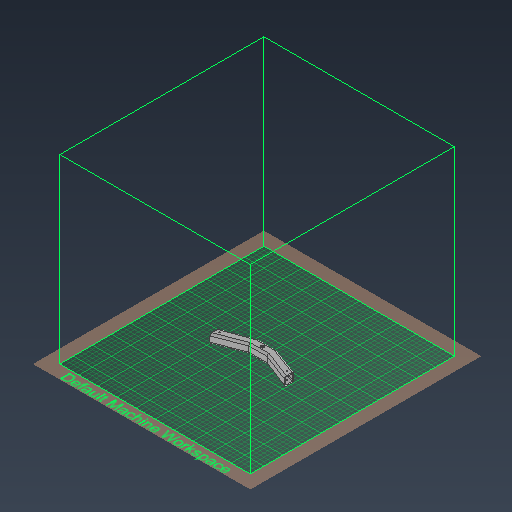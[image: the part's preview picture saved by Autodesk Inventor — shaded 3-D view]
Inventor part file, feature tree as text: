
AUTODESK INVENTOR PART (.ipt)
format: ipt  version: 2021 (Build 250183000, 183)  size: 565,760 bytes
history: native  units: mm
features: extrude x10, sketch x10, fillet x2, shell x1
ambient origin geometry x8: Origin, YZ Plane, XZ Plane, XY Plane, X Axis, Y Axis, Z Axis, Center Point
bodies: Volumenkörper1 (feature_tree)
feature tree (23):
  extrude  "Extrusion1"  Depth=66.0mm
  fillet  "Rundung3"  Radius=66.0mm
  shell  "Wandung3"  Thickness=3.490659mm
  extrude  "Extrusion8"  Depth=20.0mm
  extrude  "Extrusion9"  Depth=12.0mm
  extrude  "Extrusion10"  Depth=15.0mm
  fillet  "Rundung7"  Radius=3.0mm
  extrude  "Extrusion14"  Depth=12.0mm
  extrude  "Extrusion17"  Depth=3.0mm TaperAngle=0.0deg
  extrude  "Extrusion18"  Depth=12.0mm
  extrude  "Extrusion19"  Depth=12.0mm
  extrude  "Extrusion20"  Depth=3.0mm
  extrude  "Extrusion21"  Depth=8.5mm
  sketch  "Skizze1"  dims[d0=40.0mm d3=66.0mm d7=66.0mm d8=3.490659mm]
  sketch  "Skizze6"  dims[d9=20.0mm d10=0.0mm d19=4.0mm]
  sketch  "Skizze7"  dims[d48=2.6mm d51=12.0mm]
  sketch  "Skizze8"  dims[d52=12.0mm d53=15.0mm d55=3.0mm d56=0.0mm]
  sketch  "Skizze12"  dims[d57=12.0mm d58=12.0mm]
  sketch  "Skizze13"  dims[d59=15.0mm d61=3.0mm d62=0.0mm]
  sketch  "Skizze14"  dims[d63=12.0mm d64=12.0mm]
  sketch  "Skizze15"  dims[d66=3.0mm d67=12.0mm]
  sketch  "Skizze16"  dims[d68=12.0mm d70=3.0mm]
  sketch  "Skizze17"  dims[d71=3.0mm d72=0.0mm d73=2.0mm d87=10.0mm d89=3.490659mm d92=10.0mm d95=40.0mm d98=4.0mm d99=4.0mm d106=21.216mm d107=21.216mm d108=3.2mm d109=8.0mm d110=24.0mm d111=3.490659mm d112=3.2mm d113=8.0mm d114=27.925268mm d115=5.0mm d116=0.0mm d117=4.0mm d118=4.0mm d119=9.0mm d120=9.0mm d125=12.0mm d126=12.0mm d127=10.0mm d128=0.0mm d129=10.0mm d130=0.0mm d131=7.0mm d132=1.0mm d133=0.0mm d134=3.2mm d135=1.0mm d136=0.0mm d137=17.0mm d138=8.5mm d139=8.5mm d140=1.0mm d141=0.0mm]
